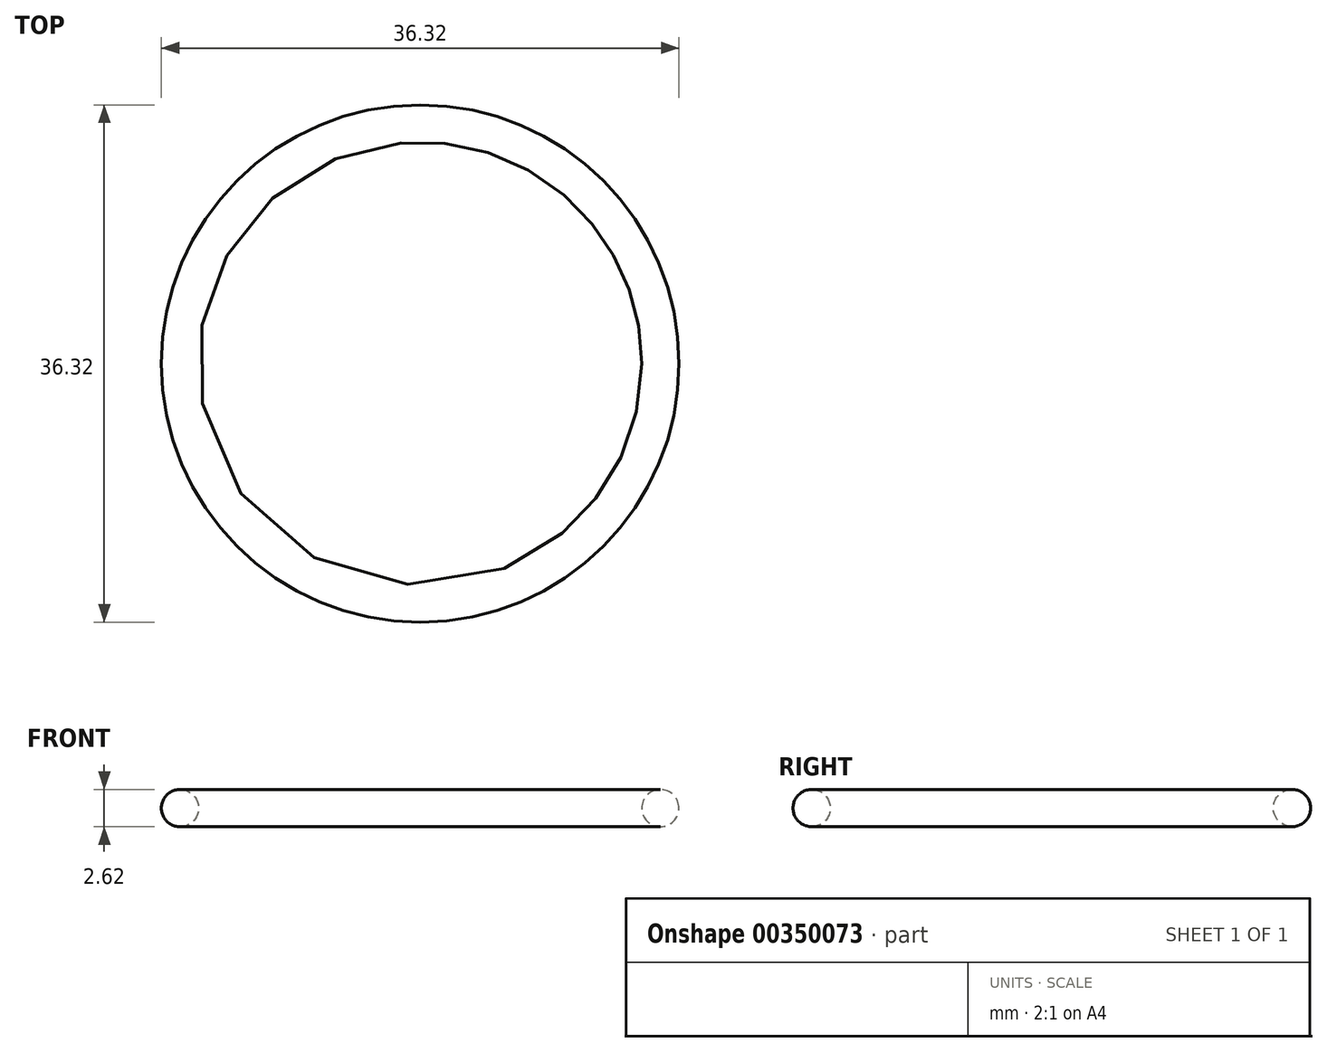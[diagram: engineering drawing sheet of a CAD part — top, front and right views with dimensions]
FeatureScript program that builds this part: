
annotation { "Feature Type Name" : "Feature", "Feature Type Description" : "" }
export const myFeature = defineFeature(function(context is Context, id is Id, definition is map)
    precondition{}
    {
        {
            var Q0;
            Q0=qCreatedBy(makeId("Front.planeOp"),FACE);
            var sketch = newSketch(context, id + "F0", { "sketchPlane" : qUnion([Q0])});
            skCircle(sketch, "E0", {"center": v(16.85, 0) * mm, "radius": 1.3 * mm});
            skLineSegment(sketch, "E1", {"start": v(0, 12.87) * mm, "end": v(0, -12.96) * mm, "construction": true});
            skSolve(sketch);
        }
        {
            var Q0;
            Q0=makeQuery(id+"F0.imprint","IMPRINT",FACE,{"disambiguationData":[TD([[makeQuery(id+"F0.imprint","IMPRINT",EDGE,{"derivedFrom":sQuery(id+"F0.wireOp",EDGE,"E0")}),1.0]])]});
            var Q1;
            Q1=sQuery(id+"F0.wireOp",EDGE,"E0");
            var Q2;
            Q2=sQuery(id+"F0.wireOp",EDGE,"E1");
            revolve(context, id + "F1", {"entities" : qUnion([Q0]), "surfaceEntities" : qUnion([Q1]), "axis" : qUnion([Q2]), "revolveType" : RevolveType.FULL});
        }
    });
